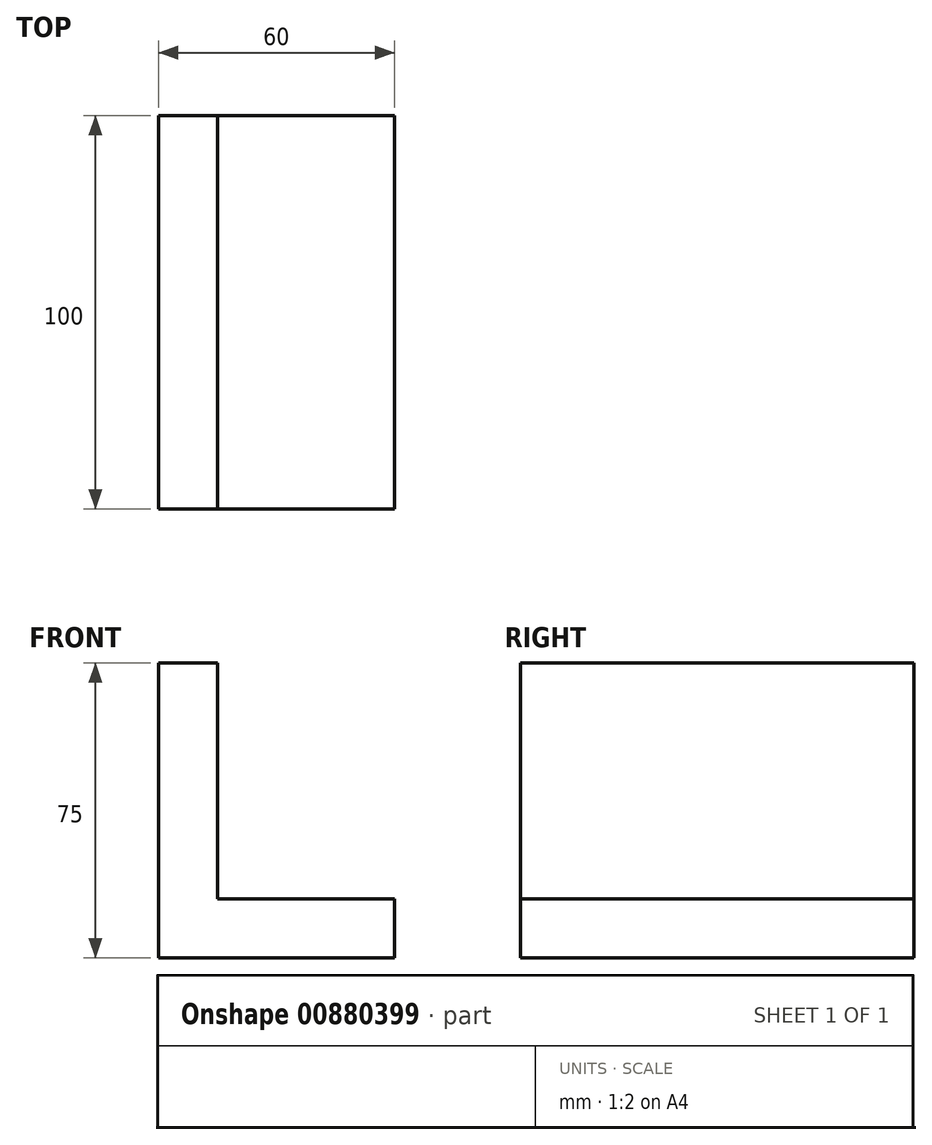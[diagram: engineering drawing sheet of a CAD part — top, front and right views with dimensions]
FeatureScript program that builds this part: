
annotation { "Feature Type Name" : "Feature", "Feature Type Description" : "" }
export const myFeature = defineFeature(function(context is Context, id is Id, definition is map)
    precondition{}
    {
        {
            var Q0;
            Q0=qCreatedBy(makeId("Front.planeOp"),FACE);
            var sketch = newSketch(context, id + "F0", { "sketchPlane" : qUnion([Q0])});
            skLineSegment(sketch, "E0", {"start": v(0, 0) * mm, "end": v(60, 0) * mm});
            skLineSegment(sketch, "E1", {"start": v(60, 0) * mm, "end": v(60, 15) * mm});
            skLineSegment(sketch, "E2", {"start": v(60, 15) * mm, "end": v(15, 15) * mm});
            skLineSegment(sketch, "E3", {"start": v(15, 75) * mm, "end": v(15, 15) * mm});
            skLineSegment(sketch, "E4", {"start": v(15, 75) * mm, "end": v(0, 75) * mm});
            skLineSegment(sketch, "E5", {"start": v(0, 75) * mm, "end": v(0, 0) * mm});
            skSolve(sketch);
        }
        {
            var Q0;
            Q0=makeQuery(id+"F0.imprint","IMPRINT",FACE,{"disambiguationData":[TD([[makeQuery(id+"F0.imprint","IMPRINT",EDGE,{"derivedFrom":sQuery(id+"F0.wireOp",EDGE,"E0")}),1.0]])]});
            extrude(context, id + "F1", {"entities" : qUnion([Q0]), "depth" : 100 * mm, "offsetDistance" : 25 * mm});
        }
    });
